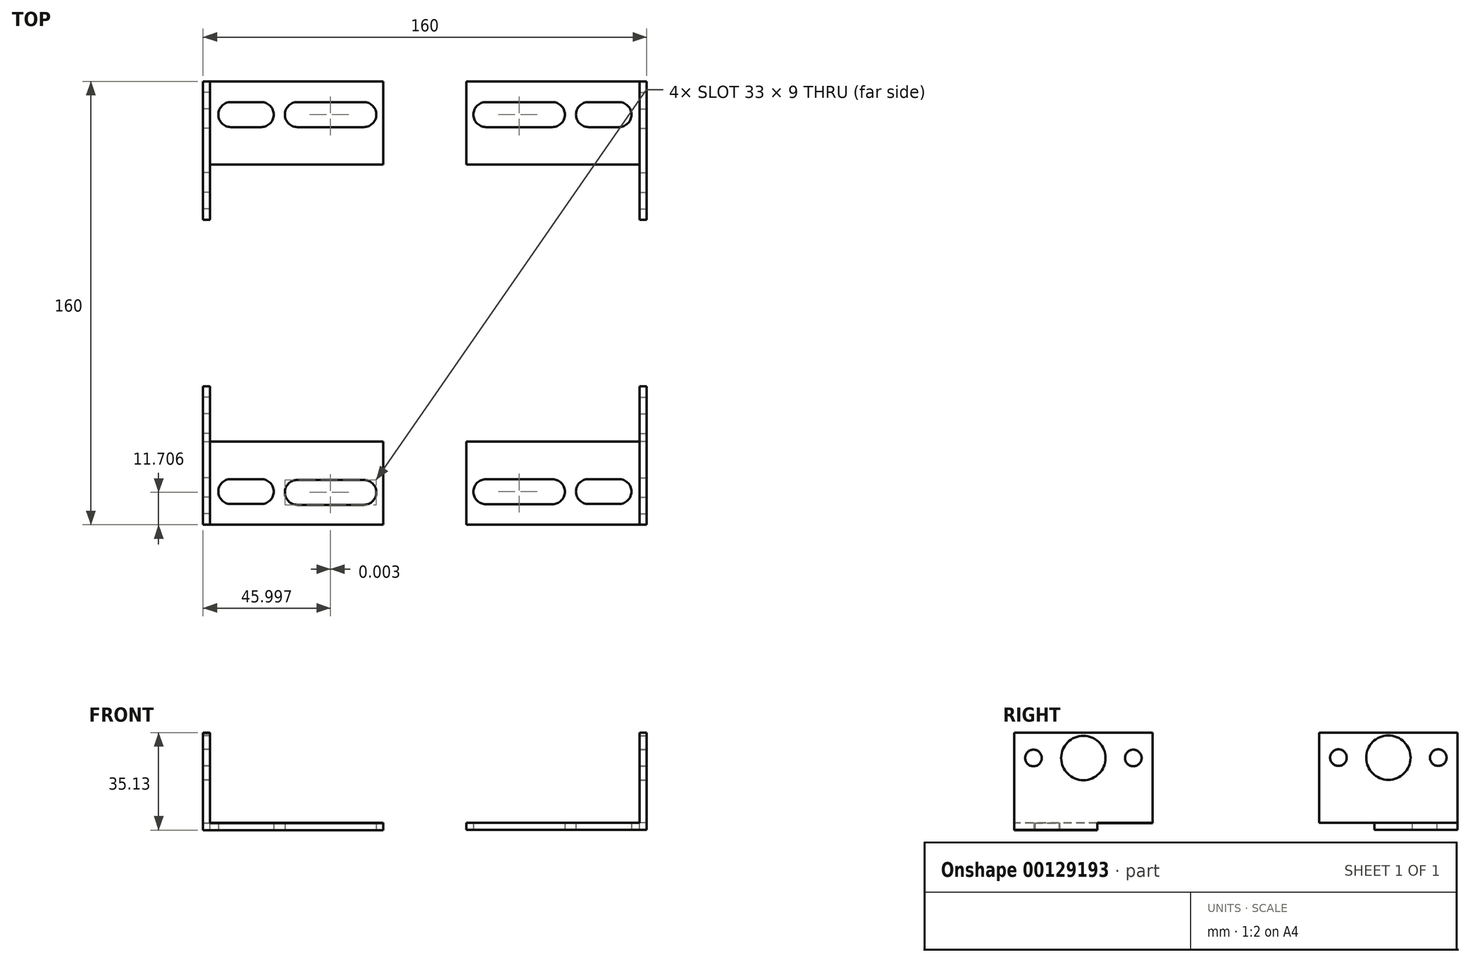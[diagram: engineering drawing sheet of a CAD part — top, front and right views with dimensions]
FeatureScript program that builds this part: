
annotation { "Feature Type Name" : "Feature", "Feature Type Description" : "" }
export const myFeature = defineFeature(function(context is Context, id is Id, definition is map)
    precondition{}
    {
        {
            var Q0;
            Q0=qCreatedBy(makeId("Front.planeOp"),FACE);
            cPlane(context, id + "F0", {"entities" : qUnion([Q0]), "cplaneType" : CPlaneType.OFFSET, "offset" : 80 * mm, "width" : 150 * mm, "height" : 150 * mm});
        }
        {
            var Q0;
            Q0=qCreatedBy(makeId("Front.planeOp"),FACE);
            cPlane(context, id + "F1", {"entities" : qUnion([Q0]), "cplaneType" : CPlaneType.OFFSET, "offset" : 80 * mm, "oppositeDirection" : true, "width" : 150 * mm, "height" : 150 * mm});
        }
        {
            var Q0;
            Q0=qCreatedBy(id+"F0.planeOp",FACE);
            var sketch = newSketch(context, id + "F2", { "sketchPlane" : qUnion([Q0])});
            skLineSegment(sketch, "E0", {"start": v(-80, 51.87) * mm, "end": v(-80, -52.13) * mm, "construction": true});
            skLineSegment(sketch, "E1.bottom", {"start": v(-80, -0.13) * mm, "end": v(-15, -0.13) * mm});
            skLineSegment(sketch, "E1.top", {"start": v(-80, 2.37) * mm, "end": v(-15, 2.37) * mm});
            skLineSegment(sketch, "E1.left", {"start": v(-80, -0.13) * mm, "end": v(-80, 2.37) * mm});
            skLineSegment(sketch, "E1.right", {"start": v(-15, -0.13) * mm, "end": v(-15, 2.37) * mm});
            skLineSegment(sketch, "E2.bottom", {"start": v(-80, -0.13) * mm, "end": v(-77.5, -0.13) * mm});
            skLineSegment(sketch, "E2.top", {"start": v(-80, 34.87) * mm, "end": v(-77.5, 34.87) * mm});
            skLineSegment(sketch, "E2.left", {"start": v(-80, -0.13) * mm, "end": v(-80, 34.87) * mm});
            skLineSegment(sketch, "E2.right", {"start": v(-77.5, -0.13) * mm, "end": v(-77.5, 34.87) * mm});
            skSolve(sketch);
        }
        {
            var Q0;
            {var subQ0=sQuery(id+"F2.wireOp",EDGE,"E1.bottom");Q0=makeQuery(id+"F2.imprint","IMPRINT",FACE,{"disambiguationData":[TD([[makeQuery(id+"F2.imprint","IMPRINT",EDGE,{"derivedFrom":subQ0}),1.0]])]});}
            var Q1;
            {var subQ5=sQuery(id+"F2.wireOp",EDGE,"E2.bottom");Q1=makeQuery(id+"F2.imprint","IMPRINT",FACE,{"disambiguationData":[TD([[makeQuery(id+"F2.imprint","IMPRINT",EDGE,{"derivedFrom":subQ5}),1.0]])]});}
            extrude(context, id + "F3", {"entities" : qUnion([Q0, Q1]), "oppositeDirection" : true, "depth" : 30 * mm});
        }
        {
            var Q0;
            {var subQ5=sQuery(id+"F2.wireOp",EDGE,"E2.top");Q0=makeQuery(id+"F2.imprint","IMPRINT",FACE,{"disambiguationData":[TD([[makeQuery(id+"F2.imprint","IMPRINT",EDGE,{"derivedFrom":subQ5}),-1.0]])]});}
            extrude(context, id + "F4", {"entities" : qUnion([Q0]), "operationType" : NewBodyOperationType.ADD, "oppositeDirection" : true, "depth" : 50 * mm});
        }
        {
            var Q0;
            {var subQ0=sQuery(id+"F2.wireOp",EDGE,"E2.left");Q0=makeQuery(id+"F4.boolean.opBoolean","MERGE",FACE,{"derivedFrom":[makeQuery(id+"F3.opExtrude","SWEPT_FACE",FACE,{"disambiguationData":[OSD([subQ0])]}),makeQuery(id+"F4.opExtrude","SWEPT_FACE",FACE,{"disambiguationData":[OSD([subQ0])]})]});}
            var sketch = newSketch(context, id + "F5", { "sketchPlane" : qUnion([Q0])});
            skCircle(sketch, "E3", {"center": v(55, 25.87) * mm, "radius": 8 * mm});
            skCircle(sketch, "E4", {"center": v(37, 25.87) * mm, "radius": 3 * mm});
            skCircle(sketch, "E5", {"center": v(73, 25.87) * mm, "radius": 3 * mm});
            skLineSegment(sketch, "E6", {"start": v(37, 25.87) * mm, "end": v(55, 25.87) * mm, "construction": true});
            skLineSegment(sketch, "E7", {"start": v(55, 25.87) * mm, "end": v(73, 25.87) * mm, "construction": true});
            skSolve(sketch);
        }
        {
            var Q0;
            Q0=makeQuery(id+"F3.opExtrude","SWEPT_FACE",FACE,{"disambiguationData":[OSD([sQuery(id+"F2.wireOp",EDGE,"E1.bottom"),sQuery(id+"F2.wireOp",EDGE,"E2.bottom")])]});
            var sketch = newSketch(context, id + "F6", { "sketchPlane" : qUnion([Q0])});
            skLineSegment(sketch, "E8", {"start": v(-95.18, 68) * mm, "end": v(-5.36, 68) * mm, "construction": true});
            skArc(sketch, "E9", {"start": v(-70, 72.5) * mm, "mid": v(-74.5, 68) * mm, "end": v(-70, 63.5) * mm});
            skArc(sketch, "E10", {"start": v(-59, 63.5) * mm, "mid": v(-54.5, 68) * mm, "end": v(-59, 72.5) * mm});
            skLineSegment(sketch, "E11", {"start": v(-70, 72.5) * mm, "end": v(-59, 72.5) * mm});
            skLineSegment(sketch, "E12", {"start": v(-59, 63.5) * mm, "end": v(-70, 63.5) * mm});
            skArc(sketch, "E13", {"start": v(-46, 72.8) * mm, "mid": v(-50.5, 68.3) * mm, "end": v(-46, 63.8) * mm});
            skArc(sketch, "E14", {"start": v(-22, 63.8) * mm, "mid": v(-17.5, 68.3) * mm, "end": v(-22, 72.8) * mm});
            skLineSegment(sketch, "E15", {"start": v(-46, 72.8) * mm, "end": v(-22, 72.8) * mm});
            skLineSegment(sketch, "E16", {"start": v(-22, 63.8) * mm, "end": v(-46, 63.8) * mm});
            skSolve(sketch);
        }
        {
            var Q0;
            Q0=makeQuery(id+"F5.imprint","IMPRINT",FACE,{"disambiguationData":[TD([[makeQuery(id+"F5.imprint","IMPRINT",EDGE,{"derivedFrom":sQuery(id+"F5.wireOp",EDGE,"E4")}),1.0]])]});
            var Q1;
            Q1=makeQuery(id+"F5.imprint","IMPRINT",FACE,{"disambiguationData":[TD([[makeQuery(id+"F5.imprint","IMPRINT",EDGE,{"derivedFrom":sQuery(id+"F5.wireOp",EDGE,"E3")}),1.0]])]});
            var Q2;
            Q2=makeQuery(id+"F5.imprint","IMPRINT",FACE,{"disambiguationData":[TD([[makeQuery(id+"F5.imprint","IMPRINT",EDGE,{"derivedFrom":sQuery(id+"F5.wireOp",EDGE,"E5")}),1.0]])]});
            extrude(context, id + "F7", {"entities" : qUnion([Q0, Q1, Q2]), "operationType" : NewBodyOperationType.REMOVE, "endBound" : BoundingType.SYMMETRIC, "oppositeDirection" : true, "depth" : 10 * mm});
        }
        {
            var Q0;
            Q0=makeQuery(id+"F6.imprint","IMPRINT",FACE,{"disambiguationData":[TD([[makeQuery(id+"F6.imprint","IMPRINT",EDGE,{"derivedFrom":sQuery(id+"F6.wireOp",EDGE,"E9")}),1.0]])]});
            var Q1;
            Q1=makeQuery(id+"F6.imprint","IMPRINT",FACE,{"disambiguationData":[TD([[makeQuery(id+"F6.imprint","IMPRINT",EDGE,{"derivedFrom":sQuery(id+"F6.wireOp",EDGE,"E13")}),1.0]])]});
            extrude(context, id + "F8", {"entities" : qUnion([Q0, Q1]), "operationType" : NewBodyOperationType.REMOVE, "endBound" : BoundingType.SYMMETRIC, "oppositeDirection" : true, "depth" : 10 * mm});
        }
        {
            var Q0;
            Q0=qCreatedBy(id+"F0.planeOp",FACE);
            var sketch = newSketch(context, id + "F9", { "sketchPlane" : qUnion([Q0])});
            skLineSegment(sketch, "E17", {"start": v(80, 51.88) * mm, "end": v(80, -53.78) * mm, "construction": true});
            skLineSegment(sketch, "E18.bottom", {"start": v(80, 0) * mm, "end": v(15, 0) * mm});
            skLineSegment(sketch, "E18.top", {"start": v(80, 2.5) * mm, "end": v(15, 2.5) * mm});
            skLineSegment(sketch, "E18.left", {"start": v(80, 0) * mm, "end": v(80, 2.5) * mm});
            skLineSegment(sketch, "E18.right", {"start": v(15, 0) * mm, "end": v(15, 2.5) * mm});
            skLineSegment(sketch, "E19.bottom", {"start": v(80, 0) * mm, "end": v(77.5, 0) * mm});
            skLineSegment(sketch, "E19.top", {"start": v(80, 35) * mm, "end": v(77.5, 35) * mm});
            skLineSegment(sketch, "E19.left", {"start": v(80, 0) * mm, "end": v(80, 35) * mm});
            skLineSegment(sketch, "E19.right", {"start": v(77.5, 0) * mm, "end": v(77.5, 35) * mm});
            skSolve(sketch);
        }
        {
            var Q0;
            {var subQ0=sQuery(id+"F9.wireOp",EDGE,"E18.bottom");Q0=makeQuery(id+"F9.imprint","IMPRINT",FACE,{"disambiguationData":[TD([[makeQuery(id+"F9.imprint","IMPRINT",EDGE,{"derivedFrom":subQ0}),-1.0]])]});}
            var Q1;
            {var subQ5=sQuery(id+"F9.wireOp",EDGE,"E19.bottom");Q1=makeQuery(id+"F9.imprint","IMPRINT",FACE,{"disambiguationData":[TD([[makeQuery(id+"F9.imprint","IMPRINT",EDGE,{"derivedFrom":subQ5}),-1.0]])]});}
            extrude(context, id + "F10", {"entities" : qUnion([Q0, Q1]), "oppositeDirection" : true, "depth" : 30 * mm});
        }
        {
            var Q0;
            {var subQ5=sQuery(id+"F9.wireOp",EDGE,"E19.top");Q0=makeQuery(id+"F9.imprint","IMPRINT",FACE,{"disambiguationData":[TD([[makeQuery(id+"F9.imprint","IMPRINT",EDGE,{"derivedFrom":subQ5}),1.0]])]});}
            extrude(context, id + "F11", {"entities" : qUnion([Q0]), "operationType" : NewBodyOperationType.ADD, "oppositeDirection" : true, "depth" : 50 * mm});
        }
        {
            var Q0;
            {var subQ0=sQuery(id+"F9.wireOp",EDGE,"E19.left");Q0=makeQuery(id+"F11.boolean.opBoolean","MERGE",FACE,{"derivedFrom":[makeQuery(id+"F10.opExtrude","SWEPT_FACE",FACE,{"disambiguationData":[OSD([subQ0])]}),makeQuery(id+"F11.opExtrude","SWEPT_FACE",FACE,{"disambiguationData":[OSD([subQ0])]})]});}
            var sketch = newSketch(context, id + "F12", { "sketchPlane" : qUnion([Q0])});
            skCircle(sketch, "E20", {"center": v(-55, 25.87) * mm, "radius": 8 * mm});
            skCircle(sketch, "E21", {"center": v(-73, 25.87) * mm, "radius": 3 * mm});
            skCircle(sketch, "E22", {"center": v(-37, 25.87) * mm, "radius": 3 * mm});
            skLineSegment(sketch, "E23", {"start": v(-73, 25.87) * mm, "end": v(-55, 25.87) * mm, "construction": true});
            skLineSegment(sketch, "E24", {"start": v(-55, 25.87) * mm, "end": v(-37, 25.87) * mm, "construction": true});
            skSolve(sketch);
        }
        {
            var Q0;
            Q0=makeQuery(id+"F10.opExtrude","SWEPT_FACE",FACE,{"disambiguationData":[OSD([sQuery(id+"F9.wireOp",EDGE,"E18.bottom"),sQuery(id+"F9.wireOp",EDGE,"E19.bottom")])]});
            var sketch = newSketch(context, id + "F13", { "sketchPlane" : qUnion([Q0])});
            skArc(sketch, "E25", {"start": v(59, 72.5) * mm, "mid": v(54.5, 68) * mm, "end": v(59, 63.5) * mm});
            skArc(sketch, "E26", {"start": v(70, 63.5) * mm, "mid": v(74.5, 68) * mm, "end": v(70, 72.5) * mm});
            skLineSegment(sketch, "E27", {"start": v(59, 72.5) * mm, "end": v(70, 72.5) * mm});
            skLineSegment(sketch, "E28", {"start": v(70, 63.5) * mm, "end": v(59, 63.5) * mm});
            skLineSegment(sketch, "E29", {"start": v(6.15, 68) * mm, "end": v(93.5, 68) * mm, "construction": true});
            skArc(sketch, "E30", {"start": v(22, 72.56) * mm, "mid": v(17.5, 68.06) * mm, "end": v(22, 63.56) * mm});
            skArc(sketch, "E31", {"start": v(46, 63.56) * mm, "mid": v(50.5, 68.06) * mm, "end": v(46, 72.56) * mm});
            skLineSegment(sketch, "E32", {"start": v(22, 72.56) * mm, "end": v(46, 72.56) * mm});
            skLineSegment(sketch, "E33", {"start": v(46, 63.56) * mm, "end": v(22, 63.56) * mm});
            skSolve(sketch);
        }
        {
            var Q0;
            Q0=makeQuery(id+"F12.imprint","IMPRINT",FACE,{"disambiguationData":[TD([[makeQuery(id+"F12.imprint","IMPRINT",EDGE,{"derivedFrom":sQuery(id+"F12.wireOp",EDGE,"E21")}),1.0]])]});
            var Q1;
            Q1=makeQuery(id+"F12.imprint","IMPRINT",FACE,{"disambiguationData":[TD([[makeQuery(id+"F12.imprint","IMPRINT",EDGE,{"derivedFrom":sQuery(id+"F12.wireOp",EDGE,"E20")}),1.0]])]});
            var Q2;
            Q2=makeQuery(id+"F12.imprint","IMPRINT",FACE,{"disambiguationData":[TD([[makeQuery(id+"F12.imprint","IMPRINT",EDGE,{"derivedFrom":sQuery(id+"F12.wireOp",EDGE,"E22")}),1.0]])]});
            extrude(context, id + "F14", {"entities" : qUnion([Q0, Q1, Q2]), "operationType" : NewBodyOperationType.REMOVE, "endBound" : BoundingType.SYMMETRIC, "oppositeDirection" : true, "depth" : 10 * mm});
        }
        {
            var Q0;
            Q0=makeQuery(id+"F13.imprint","IMPRINT",FACE,{"disambiguationData":[TD([[makeQuery(id+"F13.imprint","IMPRINT",EDGE,{"derivedFrom":sQuery(id+"F13.wireOp",EDGE,"E30")}),1.0]])]});
            var Q1;
            Q1=makeQuery(id+"F13.imprint","IMPRINT",FACE,{"disambiguationData":[TD([[makeQuery(id+"F13.imprint","IMPRINT",EDGE,{"derivedFrom":sQuery(id+"F13.wireOp",EDGE,"E25")}),1.0]])]});
            extrude(context, id + "F15", {"entities" : qUnion([Q0, Q1]), "operationType" : NewBodyOperationType.REMOVE, "endBound" : BoundingType.SYMMETRIC, "oppositeDirection" : true, "depth" : 10 * mm});
        }
        {
            var Q0;
            Q0=qCreatedBy(id+"F1.planeOp",FACE);
            var sketch = newSketch(context, id + "F16", { "sketchPlane" : qUnion([Q0])});
            skLineSegment(sketch, "E34", {"start": v(-80, 57.72) * mm, "end": v(-80, -28.34) * mm, "construction": true});
            skLineSegment(sketch, "E35.bottom", {"start": v(-80, 0) * mm, "end": v(-77.5, 0) * mm});
            skLineSegment(sketch, "E35.top", {"start": v(-80, 35) * mm, "end": v(-77.5, 35) * mm});
            skLineSegment(sketch, "E35.left", {"start": v(-80, 0) * mm, "end": v(-80, 35) * mm});
            skLineSegment(sketch, "E35.right", {"start": v(-77.5, 0) * mm, "end": v(-77.5, 35) * mm});
            skLineSegment(sketch, "E36.bottom", {"start": v(-80, 0) * mm, "end": v(-15, 0) * mm});
            skLineSegment(sketch, "E36.top", {"start": v(-80, 2.5) * mm, "end": v(-15, 2.5) * mm});
            skLineSegment(sketch, "E36.left", {"start": v(-80, 0) * mm, "end": v(-80, 2.5) * mm});
            skLineSegment(sketch, "E36.right", {"start": v(-15, 0) * mm, "end": v(-15, 2.5) * mm});
            skSolve(sketch);
        }
        {
            var Q0;
            {var subQ5=sQuery(id+"F16.wireOp",EDGE,"E36.right");Q0=makeQuery(id+"F16.imprint","IMPRINT",FACE,{"disambiguationData":[TD([[makeQuery(id+"F16.imprint","IMPRINT",EDGE,{"derivedFrom":subQ5}),1.0]])]});}
            var Q1;
            {var subQ5=sQuery(id+"F16.wireOp",EDGE,"E36.left");Q1=makeQuery(id+"F16.imprint","IMPRINT",FACE,{"disambiguationData":[TD([[makeQuery(id+"F16.imprint","IMPRINT",EDGE,{"derivedFrom":subQ5}),-1.0]])]});}
            extrude(context, id + "F17", {"entities" : qUnion([Q0, Q1]), "depth" : 30 * mm});
        }
        {
            var Q0;
            {var subQ0=sQuery(id+"F16.wireOp",EDGE,"E35.top");Q0=makeQuery(id+"F16.imprint","IMPRINT",FACE,{"disambiguationData":[TD([[makeQuery(id+"F16.imprint","IMPRINT",EDGE,{"derivedFrom":subQ0}),-1.0]])]});}
            extrude(context, id + "F18", {"entities" : qUnion([Q0]), "operationType" : NewBodyOperationType.ADD, "depth" : 50 * mm});
        }
        {
            var Q0;
            Q0=makeQuery(id+"F18.boolean.opBoolean","MERGE",FACE,{"derivedFrom":[makeQuery(id+"F17.opExtrude","SWEPT_FACE",FACE,{"disambiguationData":[OSD([sQuery(id+"F16.wireOp",EDGE,"E36.left")])]}),makeQuery(id+"F18.opExtrude","SWEPT_FACE",FACE,{"disambiguationData":[OSD([sQuery(id+"F16.wireOp",EDGE,"E35.left")])]})]});
            var sketch = newSketch(context, id + "F19", { "sketchPlane" : qUnion([Q0])});
            skLineSegment(sketch, "E37", {"start": v(-96.06, 26) * mm, "end": v(-5.53, 26) * mm, "construction": true});
            skCircle(sketch, "E38", {"center": v(-55, 26) * mm, "radius": 8 * mm});
            skCircle(sketch, "E39", {"center": v(-73, 26) * mm, "radius": 3 * mm});
            skCircle(sketch, "E40", {"center": v(-37, 26) * mm, "radius": 3 * mm});
            skSolve(sketch);
        }
        {
            var Q0;
            Q0=makeQuery(id+"F17.opExtrude","SWEPT_FACE",FACE,{"disambiguationData":[OSD([sQuery(id+"F16.wireOp",EDGE,"E36.bottom")])]});
            var sketch = newSketch(context, id + "F20", { "sketchPlane" : qUnion([Q0])});
            skLineSegment(sketch, "E41", {"start": v(-92.33, -68) * mm, "end": v(6.09, -68) * mm, "construction": true});
            skArc(sketch, "E42", {"start": v(-70, -63.5) * mm, "mid": v(-74.5, -68) * mm, "end": v(-70, -72.5) * mm});
            skArc(sketch, "E43", {"start": v(-59, -72.5) * mm, "mid": v(-54.5, -68) * mm, "end": v(-59, -63.5) * mm});
            skArc(sketch, "E44", {"start": v(-46, -63.5) * mm, "mid": v(-50.5, -68) * mm, "end": v(-46, -72.5) * mm});
            skArc(sketch, "E45", {"start": v(-22, -72.5) * mm, "mid": v(-17.5, -68) * mm, "end": v(-22, -63.5) * mm});
            skLineSegment(sketch, "E46", {"start": v(-70, -63.5) * mm, "end": v(-59, -63.5) * mm});
            skLineSegment(sketch, "E47", {"start": v(-70, -72.5) * mm, "end": v(-59, -72.5) * mm});
            skLineSegment(sketch, "E48", {"start": v(-46, -72.5) * mm, "end": v(-22, -72.5) * mm});
            skLineSegment(sketch, "E49", {"start": v(-46, -63.5) * mm, "end": v(-22, -63.5) * mm});
            skSolve(sketch);
        }
        {
            var Q0;
            Q0=makeQuery(id+"F19.imprint","IMPRINT",FACE,{"disambiguationData":[TD([[makeQuery(id+"F19.imprint","IMPRINT",EDGE,{"derivedFrom":sQuery(id+"F19.wireOp",EDGE,"E39")}),1.0]])]});
            var Q1;
            Q1=makeQuery(id+"F19.imprint","IMPRINT",FACE,{"disambiguationData":[TD([[makeQuery(id+"F19.imprint","IMPRINT",EDGE,{"derivedFrom":sQuery(id+"F19.wireOp",EDGE,"E38")}),1.0]])]});
            var Q2;
            Q2=makeQuery(id+"F19.imprint","IMPRINT",FACE,{"disambiguationData":[TD([[makeQuery(id+"F19.imprint","IMPRINT",EDGE,{"derivedFrom":sQuery(id+"F19.wireOp",EDGE,"E40")}),1.0]])]});
            extrude(context, id + "F21", {"entities" : qUnion([Q0, Q1, Q2]), "operationType" : NewBodyOperationType.REMOVE, "endBound" : BoundingType.SYMMETRIC, "oppositeDirection" : true, "depth" : 10 * mm});
        }
        {
            var Q0;
            Q0=makeQuery(id+"F20.imprint","IMPRINT",FACE,{"disambiguationData":[TD([[makeQuery(id+"F20.imprint","IMPRINT",EDGE,{"derivedFrom":sQuery(id+"F20.wireOp",EDGE,"E42")}),1.0]])]});
            var Q1;
            Q1=makeQuery(id+"F20.imprint","IMPRINT",FACE,{"disambiguationData":[TD([[makeQuery(id+"F20.imprint","IMPRINT",EDGE,{"derivedFrom":sQuery(id+"F20.wireOp",EDGE,"E44")}),1.0]])]});
            extrude(context, id + "F22", {"entities" : qUnion([Q0, Q1]), "operationType" : NewBodyOperationType.REMOVE, "endBound" : BoundingType.SYMMETRIC, "oppositeDirection" : true, "depth" : 10 * mm});
        }
        {
            var Q0;
            Q0=qCreatedBy(id+"F1.planeOp",FACE);
            var sketch = newSketch(context, id + "F23", { "sketchPlane" : qUnion([Q0])});
            skLineSegment(sketch, "E50", {"start": v(80, 46.17) * mm, "end": v(80, -30.71) * mm, "construction": true});
            skLineSegment(sketch, "E51.bottom", {"start": v(80, 0) * mm, "end": v(77.5, 0) * mm});
            skLineSegment(sketch, "E51.top", {"start": v(80, 35) * mm, "end": v(77.5, 35) * mm});
            skLineSegment(sketch, "E51.left", {"start": v(80, 0) * mm, "end": v(80, 35) * mm});
            skLineSegment(sketch, "E51.right", {"start": v(77.5, 0) * mm, "end": v(77.5, 35) * mm});
            skLineSegment(sketch, "E52.bottom", {"start": v(80, 0) * mm, "end": v(15, 0) * mm});
            skLineSegment(sketch, "E52.top", {"start": v(80, 2.5) * mm, "end": v(15, 2.5) * mm});
            skLineSegment(sketch, "E52.left", {"start": v(80, 0) * mm, "end": v(80, 2.5) * mm});
            skLineSegment(sketch, "E52.right", {"start": v(15, 0) * mm, "end": v(15, 2.5) * mm});
            skSolve(sketch);
        }
        {
            var Q0;
            {var subQ5=sQuery(id+"F23.wireOp",EDGE,"E52.right");Q0=makeQuery(id+"F23.imprint","IMPRINT",FACE,{"disambiguationData":[TD([[makeQuery(id+"F23.imprint","IMPRINT",EDGE,{"derivedFrom":subQ5}),-1.0]])]});}
            var Q1;
            {var subQ5=sQuery(id+"F23.wireOp",EDGE,"E52.left");Q1=makeQuery(id+"F23.imprint","IMPRINT",FACE,{"disambiguationData":[TD([[makeQuery(id+"F23.imprint","IMPRINT",EDGE,{"derivedFrom":subQ5}),1.0]])]});}
            extrude(context, id + "F24", {"entities" : qUnion([Q0, Q1]), "depth" : 30 * mm});
        }
        {
            var Q0;
            {var subQ0=sQuery(id+"F23.wireOp",EDGE,"E51.top");Q0=makeQuery(id+"F23.imprint","IMPRINT",FACE,{"disambiguationData":[TD([[makeQuery(id+"F23.imprint","IMPRINT",EDGE,{"derivedFrom":subQ0}),1.0]])]});}
            extrude(context, id + "F25", {"entities" : qUnion([Q0]), "operationType" : NewBodyOperationType.ADD, "depth" : 50 * mm});
        }
        {
            var Q0;
            Q0=makeQuery(id+"F25.boolean.opBoolean","MERGE",FACE,{"derivedFrom":[makeQuery(id+"F24.opExtrude","SWEPT_FACE",FACE,{"disambiguationData":[OSD([sQuery(id+"F23.wireOp",EDGE,"E52.left")])]}),makeQuery(id+"F25.opExtrude","SWEPT_FACE",FACE,{"disambiguationData":[OSD([sQuery(id+"F23.wireOp",EDGE,"E51.left")])]})]});
            var sketch = newSketch(context, id + "F26", { "sketchPlane" : qUnion([Q0])});
            skLineSegment(sketch, "E53", {"start": v(14.16, 26) * mm, "end": v(93.72, 26) * mm, "construction": true});
            skCircle(sketch, "E54", {"center": v(55, 26) * mm, "radius": 8 * mm});
            skCircle(sketch, "E55", {"center": v(37, 26) * mm, "radius": 3 * mm});
            skCircle(sketch, "E56", {"center": v(73, 26) * mm, "radius": 3 * mm});
            skSolve(sketch);
        }
        {
            var Q0;
            Q0=makeQuery(id+"F24.opExtrude","SWEPT_FACE",FACE,{"disambiguationData":[OSD([sQuery(id+"F23.wireOp",EDGE,"E52.bottom")])]});
            var sketch = newSketch(context, id + "F27", { "sketchPlane" : qUnion([Q0])});
            skLineSegment(sketch, "E57", {"start": v(11.2, -68) * mm, "end": v(88.39, -68) * mm, "construction": true});
            skArc(sketch, "E58", {"start": v(70, -72.5) * mm, "mid": v(74.5, -68) * mm, "end": v(70, -63.5) * mm});
            skArc(sketch, "E59", {"start": v(59, -63.5) * mm, "mid": v(54.5, -68) * mm, "end": v(59, -72.5) * mm});
            skArc(sketch, "E60", {"start": v(46, -72.5) * mm, "mid": v(50.5, -68) * mm, "end": v(46, -63.5) * mm});
            skArc(sketch, "E61", {"start": v(22, -63.5) * mm, "mid": v(17.5, -68) * mm, "end": v(22, -72.5) * mm});
            skLineSegment(sketch, "E62", {"start": v(59, -72.5) * mm, "end": v(70, -72.5) * mm});
            skLineSegment(sketch, "E63", {"start": v(59, -63.5) * mm, "end": v(70, -63.5) * mm});
            skLineSegment(sketch, "E64", {"start": v(46, -63.5) * mm, "end": v(22, -63.5) * mm});
            skLineSegment(sketch, "E65", {"start": v(22, -72.5) * mm, "end": v(46, -72.5) * mm});
            skSolve(sketch);
        }
        {
            var Q0;
            Q0=makeQuery(id+"F26.imprint","IMPRINT",FACE,{"disambiguationData":[TD([[makeQuery(id+"F26.imprint","IMPRINT",EDGE,{"derivedFrom":sQuery(id+"F26.wireOp",EDGE,"E55")}),1.0]])]});
            var Q1;
            Q1=makeQuery(id+"F26.imprint","IMPRINT",FACE,{"disambiguationData":[TD([[makeQuery(id+"F26.imprint","IMPRINT",EDGE,{"derivedFrom":sQuery(id+"F26.wireOp",EDGE,"E54")}),1.0]])]});
            var Q2;
            Q2=makeQuery(id+"F26.imprint","IMPRINT",FACE,{"disambiguationData":[TD([[makeQuery(id+"F26.imprint","IMPRINT",EDGE,{"derivedFrom":sQuery(id+"F26.wireOp",EDGE,"E56")}),1.0]])]});
            extrude(context, id + "F28", {"entities" : qUnion([Q0, Q1, Q2]), "operationType" : NewBodyOperationType.REMOVE, "endBound" : BoundingType.SYMMETRIC, "oppositeDirection" : true, "depth" : 10 * mm});
        }
        {
            var Q0;
            Q0=makeQuery(id+"F27.imprint","IMPRINT",FACE,{"disambiguationData":[TD([[makeQuery(id+"F27.imprint","IMPRINT",EDGE,{"derivedFrom":sQuery(id+"F27.wireOp",EDGE,"E60")}),1.0]])]});
            var Q1;
            Q1=makeQuery(id+"F27.imprint","IMPRINT",FACE,{"disambiguationData":[TD([[makeQuery(id+"F27.imprint","IMPRINT",EDGE,{"derivedFrom":sQuery(id+"F27.wireOp",EDGE,"E58")}),1.0]])]});
            extrude(context, id + "F29", {"entities" : qUnion([Q0, Q1]), "operationType" : NewBodyOperationType.REMOVE, "endBound" : BoundingType.SYMMETRIC, "oppositeDirection" : true, "depth" : 10 * mm});
        }
    });
